# Revit family: Emma SA-114 Chair
name_source: partatom
category: Furniture
revit_build: Autodesk Revit 2017 (Build: 20160225_1515(x64)
units: mm (PartAtom-declared; Revit-internal decimal feet)

## family parameters
Always vertical = Yes
Cut with Voids When Loaded = No
OmniClass Number = 23.40.20.00
OmniClass Title = General Furniture and Specialties
Room Calculation Point = No
Shared = No
Work Plane-Based = No

## types (1)
- Emma SA-114 Chair
    Assembly Code = E2020200
    Assistance = Call for assistance number: 336.941.3446
    Back material = Palisander or Beech Wood
    Chair type = 4-Leg
    Collection = Emma
    Depth = 20 mm
    Description = Chair with metal frame with chrome finish, upholstered seat and Palisander or Beech wood back
    Height = 32 mm  [stored 0.104987 ft]
    Industry = Café, Restaurant, Bistro, Lounge, Hotel, Club
    Length = 21 mm
    Manufacturer = Beaufurn
    Manufacturer Country = USA
    Model = Emma SA-114 Chair
    Products of collection = Emma Armchairs and Emma Barstools
    Seat depth = 19 mm  [stored 0.062336 ft]
    Seat height = 19 mm  [stored 0.062336 ft]
    Structure material = Steel
    Type Comments = Suitable for Banquet, Cafeteria, Church, Conference, Institutional, Lobby, Lounge, Office, University
    URL = http://beaufurn.com
    Upholstery material = Graded Fabric or Com
    Usage = Indoor

note: [stored X ft] marks values corroborated as IEEE doubles in the binary element streams (Revit-internal decimal feet)

## geometry (parser evidence)
native form markers: Sweep x3
no freeform markers — native parametric forms only
